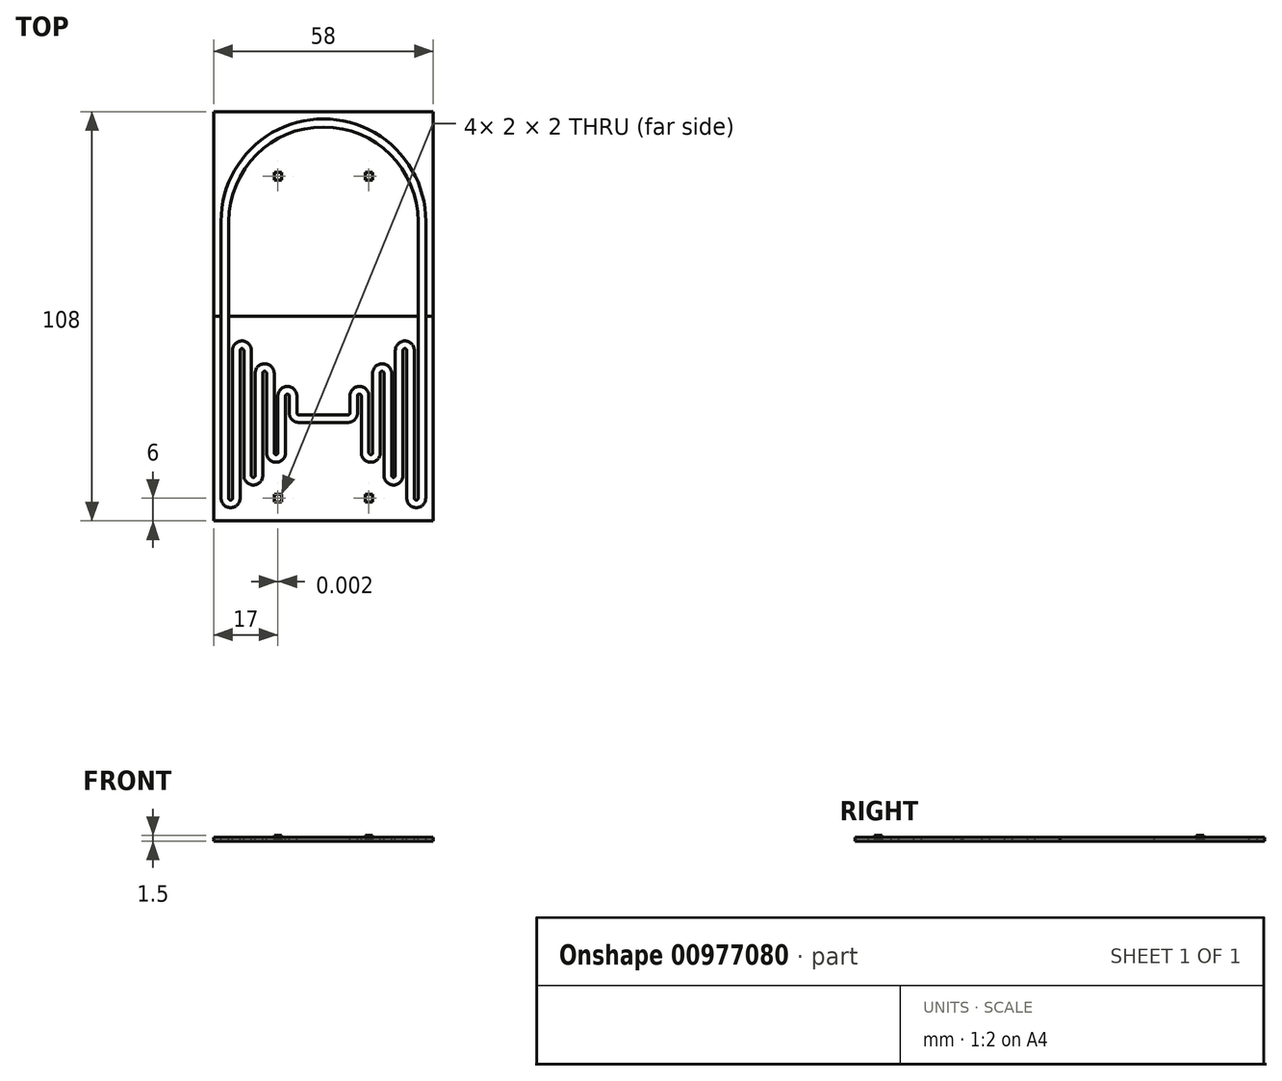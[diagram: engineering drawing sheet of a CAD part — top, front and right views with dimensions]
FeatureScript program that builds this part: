
annotation { "Feature Type Name" : "Feature", "Feature Type Description" : "" }
export const myFeature = defineFeature(function(context is Context, id is Id, definition is map)
    precondition{}
    {
        {
            var Q0;
            Q0=qCreatedBy(makeId("Top.planeOp"),FACE);
            var sketch = newSketch(context, id + "F0", { "sketchPlane" : qUnion([Q0])});
            skLineSegment(sketch, "E0.bottom", {"start": v(29, 27) * mm, "end": v(-29, 27) * mm});
            skLineSegment(sketch, "E0.top", {"start": v(29, -27) * mm, "end": v(-29, -27) * mm});
            skLineSegment(sketch, "E0.left", {"start": v(29, 27) * mm, "end": v(29, -27) * mm});
            skLineSegment(sketch, "E0.right", {"start": v(-29, 27) * mm, "end": v(-29, -27) * mm});
            skPoint(sketch, "E0.middle", {"position": v(0, 0) * mm});
            skSolve(sketch);
        }
        {
            var Q0;
            Q0=makeQuery(id+"F0.imprint","IMPRINT",FACE,{"disambiguationData":[TD([[makeQuery(id+"F0.imprint","IMPRINT",EDGE,{"derivedFrom":sQuery(id+"F0.wireOp",EDGE,"E0.bottom")}),1.0]])]});
            extrude(context, id + "F1", {"entities" : qUnion([Q0]), "depth" : 1 * mm, "offsetDistance" : 25 * mm});
        }
        {
            var Q0;
            Q0=makeQuery(id+"F1.opExtrude","CAP_FACE",FACE,{"disambiguationData":[OSD([sQuery(id+"F0.wireOp",EDGE,"E0.bottom"),sQuery(id+"F0.wireOp",EDGE,"E0.top"),sQuery(id+"F0.wireOp",EDGE,"E0.left"),sQuery(id+"F0.wireOp",EDGE,"E0.right")])],"isStart":false});
            var sketch = newSketch(context, id + "F2", { "sketchPlane" : qUnion([Q0])});
            skPoint(sketch, "E1.middle", {"position": v(-28, 0) * mm});
            skLineSegment(sketch, "E2.left", {"start": v(-27, 25) * mm, "end": v(-27, -21) * mm});
            skLineSegment(sketch, "E2.right", {"start": v(-25, 23.27) * mm, "end": v(-25, -21) * mm});
            skLineSegment(sketch, "E3.left", {"start": v(-25, 18) * mm, "end": v(-25, -21) * mm});
            skLineSegment(sketch, "E3.right", {"start": v(-24, 18) * mm, "end": v(-24, -21) * mm});
            skLineSegment(sketch, "E4.right", {"start": v(-22, 18) * mm, "end": v(-22, -21) * mm});
            skLineSegment(sketch, "E5.left", {"start": v(-21, 18) * mm, "end": v(-21, -15) * mm});
            skLineSegment(sketch, "E5.right", {"start": v(-19, 18) * mm, "end": v(-19, -15) * mm});
            skLineSegment(sketch, "E6.left", {"start": v(-18, 12) * mm, "end": v(-18, -15) * mm});
            skLineSegment(sketch, "E6.right", {"start": v(-16, 12) * mm, "end": v(-16, -15) * mm});
            skLineSegment(sketch, "E7.left", {"start": v(-15, 12) * mm, "end": v(-15, -9) * mm});
            skLineSegment(sketch, "E7.right", {"start": v(-13, 12) * mm, "end": v(-13, -9) * mm});
            skLineSegment(sketch, "E8.left", {"start": v(-12, 6) * mm, "end": v(-12, -9) * mm});
            skLineSegment(sketch, "E8.right", {"start": v(-10, 6) * mm, "end": v(-10, -9) * mm});
            skPoint(sketch, "E9.firstSnap0", {"position": v(-13, 1.5) * mm});
            skLineSegment(sketch, "E10.left", {"start": v(-9, 6) * mm, "end": v(-9, 1.5) * mm});
            skLineSegment(sketch, "E10.right", {"start": v(-7, 6) * mm, "end": v(-7, 1.5) * mm});
            skLineSegment(sketch, "E11.bottom", {"start": v(6.5, 1) * mm, "end": v(-6.5, 1) * mm});
            skLineSegment(sketch, "E11.top", {"start": v(6.5, -1) * mm, "end": v(-6.5, -1) * mm});
            skPoint(sketch, "E11.middle", {"position": v(0, 0) * mm});
            skArc(sketch, "E12", {"start": v(-9, 6) * mm, "mid": v(-9.5, 6.5) * mm, "end": v(-10, 6) * mm});
            skArc(sketch, "E13", {"start": v(-7, 6) * mm, "mid": v(-9.5, 8.5) * mm, "end": v(-12, 6) * mm});
            skArc(sketch, "E14", {"start": v(-13, -9) * mm, "mid": v(-12.5, -9.5) * mm, "end": v(-12, -9) * mm});
            skArc(sketch, "E15", {"start": v(-15, -9) * mm, "mid": v(-12.5, -11.5) * mm, "end": v(-10, -9) * mm});
            skArc(sketch, "E16", {"start": v(-15, 12) * mm, "mid": v(-15.5, 12.5) * mm, "end": v(-16, 12) * mm});
            skArc(sketch, "E17", {"start": v(-13, 12) * mm, "mid": v(-15.5, 14.5) * mm, "end": v(-18, 12) * mm});
            skArc(sketch, "E18", {"start": v(-19, -15) * mm, "mid": v(-18.5, -15.5) * mm, "end": v(-18, -15) * mm});
            skArc(sketch, "E19", {"start": v(-21, -15) * mm, "mid": v(-18.5, -17.5) * mm, "end": v(-16, -15) * mm});
            skArc(sketch, "E20", {"start": v(-21, 18) * mm, "mid": v(-21.5, 18.5) * mm, "end": v(-22, 18) * mm});
            skArc(sketch, "E21", {"start": v(-19, 18) * mm, "mid": v(-21.5, 20.5) * mm, "end": v(-24, 18) * mm});
            skArc(sketch, "E22", {"start": v(-25, -21) * mm, "mid": v(-24.5, -21.5) * mm, "end": v(-24, -21) * mm});
            skArc(sketch, "E23", {"start": v(-27, -21) * mm, "mid": v(-24.5, -23.5) * mm, "end": v(-22, -21) * mm});
            skArc(sketch, "E24", {"start": v(-7, 1.5) * mm, "mid": v(-6.86, 1.14) * mm, "end": v(-6.5, 1) * mm});
            skArc(sketch, "E25", {"start": v(-9, 1.5) * mm, "mid": v(-8.27, -0.27) * mm, "end": v(-6.5, -1) * mm});
            skLineSegment(sketch, "E26.left", {"start": v(25, 25) * mm, "end": v(25, -21) * mm});
            skLineSegment(sketch, "E26.right", {"start": v(27, 23.27) * mm, "end": v(27, -21) * mm});
            skLineSegment(sketch, "E27.right", {"start": v(25, 23.27) * mm, "end": v(25, -22.73) * mm});
            skLineSegment(sketch, "E28.left", {"start": v(22, 18) * mm, "end": v(22, -21) * mm});
            skLineSegment(sketch, "E28.right", {"start": v(24, 18) * mm, "end": v(24, -21) * mm});
            skLineSegment(sketch, "E29.left", {"start": v(19, 18) * mm, "end": v(19, -15) * mm});
            skLineSegment(sketch, "E29.right", {"start": v(21, 18) * mm, "end": v(21, -15) * mm});
            skLineSegment(sketch, "E30.left", {"start": v(16, 12) * mm, "end": v(16, -15) * mm});
            skLineSegment(sketch, "E30.right", {"start": v(18, 12) * mm, "end": v(18, -15) * mm});
            skLineSegment(sketch, "E31.right", {"start": v(16, 12) * mm, "end": v(16, -16.73) * mm});
            skLineSegment(sketch, "E32.left", {"start": v(13, 12) * mm, "end": v(13, -9) * mm});
            skLineSegment(sketch, "E32.right", {"start": v(15, 12) * mm, "end": v(15, -9) * mm});
            skLineSegment(sketch, "E33.left", {"start": v(10, 6) * mm, "end": v(10, -9) * mm});
            skLineSegment(sketch, "E33.right", {"start": v(12, 6) * mm, "end": v(12, -9) * mm});
            skLineSegment(sketch, "E34.left", {"start": v(7, 6) * mm, "end": v(7, 1.5) * mm});
            skLineSegment(sketch, "E34.right", {"start": v(9, 6) * mm, "end": v(9, 1.5) * mm});
            skArc(sketch, "E35", {"start": v(6.5, 1) * mm, "mid": v(6.85, 1.14) * mm, "end": v(7, 1.5) * mm});
            skArc(sketch, "E36", {"start": v(6.5, -1) * mm, "mid": v(8.26, -0.27) * mm, "end": v(9, 1.5) * mm});
            skArc(sketch, "E37", {"start": v(22, -21) * mm, "mid": v(24.5, -23.5) * mm, "end": v(27, -21) * mm});
            skArc(sketch, "E38", {"start": v(24, -21) * mm, "mid": v(24.5, -21.5) * mm, "end": v(25, -21) * mm});
            skArc(sketch, "E39", {"start": v(18, -15) * mm, "mid": v(18.5, -15.5) * mm, "end": v(19, -15) * mm});
            skArc(sketch, "E40", {"start": v(16, -15) * mm, "mid": v(18.5, -17.5) * mm, "end": v(21, -15) * mm});
            skArc(sketch, "E41", {"start": v(12, -9) * mm, "mid": v(12.5, -9.5) * mm, "end": v(13, -9) * mm});
            skArc(sketch, "E42", {"start": v(10, -9) * mm, "mid": v(12.5, -11.5) * mm, "end": v(15, -9) * mm});
            skArc(sketch, "E43", {"start": v(22, 18) * mm, "mid": v(21.5, 18.5) * mm, "end": v(21, 18) * mm});
            skArc(sketch, "E44", {"start": v(24, 18) * mm, "mid": v(21.5, 20.5) * mm, "end": v(19, 18) * mm});
            skArc(sketch, "E45", {"start": v(16, 12) * mm, "mid": v(15.5, 12.5) * mm, "end": v(15, 12) * mm});
            skArc(sketch, "E46", {"start": v(18, 12) * mm, "mid": v(15.5, 14.5) * mm, "end": v(13, 12) * mm});
            skArc(sketch, "E47", {"start": v(10, 6) * mm, "mid": v(9.5, 6.5) * mm, "end": v(9, 6) * mm});
            skArc(sketch, "E48", {"start": v(12, 6) * mm, "mid": v(9.5, 8.5) * mm, "end": v(7, 6) * mm});
            skLineSegment(sketch, "E49.top", {"start": v(-27, 27) * mm, "end": v(-25, 27) * mm});
            skLineSegment(sketch, "E49.left", {"start": v(-27, 25) * mm, "end": v(-27, 27) * mm});
            skLineSegment(sketch, "E49.right", {"start": v(-25, 25) * mm, "end": v(-25, 27) * mm});
            skLineSegment(sketch, "E50.top", {"start": v(25, 27) * mm, "end": v(27, 27) * mm});
            skLineSegment(sketch, "E50.left", {"start": v(25, 23.27) * mm, "end": v(25, 27) * mm});
            skLineSegment(sketch, "E50.right", {"start": v(27, 25) * mm, "end": v(27, 27) * mm});
            skLineSegment(sketch, "E51", {"start": v(27, 25) * mm, "end": v(27, 23.27) * mm});
            skLineSegment(sketch, "E52", {"start": v(-25, 25) * mm, "end": v(-25, 23.27) * mm});
            skSolve(sketch);
        }
        {
            var Q0;
            Q0=makeQuery(id+"F2.imprint","IMPRINT",FACE,{"disambiguationData":[TD([[makeQuery(id+"F2.imprint","IMPRINT",EDGE,{"derivedFrom":sQuery(id+"F2.wireOp",EDGE,"E2.left")}),1.0]])]});
            extrude(context, id + "F3", {"entities" : qUnion([Q0]), "operationType" : NewBodyOperationType.REMOVE, "oppositeDirection" : true, "depth" : 1 * mm, "offsetDistance" : 25 * mm});
        }
        {
            var Q0;
            Q0=qCreatedBy(makeId("Top.planeOp"),FACE);
            var sketch = newSketch(context, id + "F4", { "sketchPlane" : qUnion([Q0])});
            skLineSegment(sketch, "E53.bottom", {"start": v(-29, 27) * mm, "end": v(29, 27) * mm});
            skLineSegment(sketch, "E53.top", {"start": v(-29, 81) * mm, "end": v(29, 81) * mm});
            skLineSegment(sketch, "E53.left", {"start": v(-29, 27) * mm, "end": v(-29, 81) * mm});
            skLineSegment(sketch, "E53.right", {"start": v(29, 27) * mm, "end": v(29, 81) * mm});
            skSolve(sketch);
        }
        {
            var Q0;
            Q0=makeQuery(id+"F4.imprint","IMPRINT",FACE,{"disambiguationData":[TD([[makeQuery(id+"F4.imprint","IMPRINT",EDGE,{"derivedFrom":sQuery(id+"F4.wireOp",EDGE,"E53.bottom")}),1.0]])]});
            extrude(context, id + "F5", {"entities" : qUnion([Q0]), "depth" : 1 * mm, "offsetDistance" : 25 * mm});
        }
        {
            var Q0;
            Q0=makeQuery(id+"F5.opExtrude","CAP_FACE",FACE,{"disambiguationData":[OSD([sQuery(id+"F4.wireOp",EDGE,"E53.bottom"),sQuery(id+"F4.wireOp",EDGE,"E53.top"),sQuery(id+"F4.wireOp",EDGE,"E53.left"),sQuery(id+"F4.wireOp",EDGE,"E53.right")])],"isStart":false});
            var sketch = newSketch(context, id + "F6", { "sketchPlane" : qUnion([Q0])});
            skLineSegment(sketch, "E54.bottom", {"start": v(-27, 27) * mm, "end": v(-25, 27) * mm});
            skLineSegment(sketch, "E54.top", {"start": v(-27, 52) * mm, "end": v(-25, 52) * mm});
            skLineSegment(sketch, "E54.left", {"start": v(-27, 27) * mm, "end": v(-27, 52) * mm});
            skLineSegment(sketch, "E54.right", {"start": v(-25, 27) * mm, "end": v(-25, 52) * mm});
            skLineSegment(sketch, "E55.bottom", {"start": v(27, 27) * mm, "end": v(25, 27) * mm});
            skLineSegment(sketch, "E55.top", {"start": v(27, 52) * mm, "end": v(25, 52) * mm});
            skLineSegment(sketch, "E55.left", {"start": v(27, 27) * mm, "end": v(27, 52) * mm});
            skLineSegment(sketch, "E55.right", {"start": v(25, 27) * mm, "end": v(25, 52) * mm});
            skArc(sketch, "E56", {"start": v(25, 52) * mm, "mid": v(0, 77) * mm, "end": v(-25, 52) * mm});
            skArc(sketch, "E57", {"start": v(27, 52) * mm, "mid": v(0, 79.13) * mm, "end": v(-27, 52) * mm});
            skPoint(sketch, "E57.startSnap0", {"position": v(27, 39.5) * mm});
            skSolve(sketch);
        }
        {
            var Q0;
            Q0=qSketchRegion(id+"F6",true);
            extrude(context, id + "F7", {"entities" : qUnion([Q0]), "operationType" : NewBodyOperationType.REMOVE, "oppositeDirection" : true, "depth" : 1 * mm, "offsetDistance" : 25 * mm});
        }
        {
            var Q0;
            Q0=makeQuery(id+"F2.imprint","IMPRINT",FACE,{"disambiguationData":[TD([[makeQuery(id+"F2.imprint","IMPRINT",EDGE,{"derivedFrom":sQuery(id+"F2.wireOp",EDGE,"E2.left")}),-1.0]])]});
            var sketch = newSketch(context, id + "F8", { "sketchPlane" : qUnion([Q0])});
            skLineSegment(sketch, "E58.bottom", {"start": v(-13, -20) * mm, "end": v(-11, -20) * mm});
            skLineSegment(sketch, "E58.top", {"start": v(-13, -22) * mm, "end": v(-11, -22) * mm});
            skLineSegment(sketch, "E58.left", {"start": v(-13, -20) * mm, "end": v(-13, -22) * mm});
            skLineSegment(sketch, "E58.right", {"start": v(-11, -20) * mm, "end": v(-11, -22) * mm});
            skLineSegment(sketch, "E59.bottom", {"start": v(11, -20) * mm, "end": v(13, -20) * mm});
            skLineSegment(sketch, "E59.top", {"start": v(11, -22) * mm, "end": v(13, -22) * mm});
            skLineSegment(sketch, "E59.left", {"start": v(11, -20) * mm, "end": v(11, -22) * mm});
            skLineSegment(sketch, "E59.right", {"start": v(13, -20) * mm, "end": v(13, -22) * mm});
            skSolve(sketch);
        }
        {
            var Q0;
            Q0 = qSketchRegion(id + "F8", true);
            extrude(context, id + "F9", {"entities" : qUnion([Q0]), "operationType" : NewBodyOperationType.ADD, "depth" : 0.5 * mm, "offsetDistance" : 25 * mm});
        }
        {
            var Q0;
            {var subQ0=sQuery(id+"F4.wireOp",EDGE,"E53.bottom");Q0=makeQuery(id+"F7.boolean.opBoolean","SPLIT",FACE,{"disambiguationData":[TD([makeQuery(id+"F7.opExtrude","SWEPT_FACE",FACE,{"disambiguationData":[OSD([sQuery(id+"F6.wireOp",EDGE,"E55.top")])]})])],"derivedFrom":makeQuery(id+"F5.opExtrude","CAP_FACE",FACE,{"disambiguationData":[OSD([subQ0,sQuery(id+"F4.wireOp",EDGE,"E53.top"),sQuery(id+"F4.wireOp",EDGE,"E53.left"),sQuery(id+"F4.wireOp",EDGE,"E53.right")])],"isStart":false})});}
            var sketch = newSketch(context, id + "F10", { "sketchPlane" : qUnion([Q0])});
            skLineSegment(sketch, "E60.bottom", {"start": v(-13, 65) * mm, "end": v(-11, 65) * mm});
            skLineSegment(sketch, "E60.top", {"start": v(-13, 63) * mm, "end": v(-11, 63) * mm});
            skLineSegment(sketch, "E60.left", {"start": v(-13, 65) * mm, "end": v(-13, 63) * mm});
            skLineSegment(sketch, "E60.right", {"start": v(-11, 65) * mm, "end": v(-11, 63) * mm});
            skLineSegment(sketch, "E61.bottom", {"start": v(11, 65) * mm, "end": v(13, 65) * mm});
            skLineSegment(sketch, "E61.top", {"start": v(11, 63) * mm, "end": v(13, 63) * mm});
            skLineSegment(sketch, "E61.left", {"start": v(11, 65) * mm, "end": v(11, 63) * mm});
            skLineSegment(sketch, "E61.right", {"start": v(13, 65) * mm, "end": v(13, 63) * mm});
            skSolve(sketch);
        }
        {
            var Q0;
            Q0 = qSketchRegion(id + "F10", true);
            extrude(context, id + "F11", {"entities" : qUnion([Q0]), "operationType" : NewBodyOperationType.ADD, "depth" : 0.5 * mm, "offsetDistance" : 25 * mm});
        }
        {
            var Q0;
            {var subQ0=sQuery(id+"F4.wireOp",EDGE,"E53.bottom");Q0=makeQuery(id+"F7.boolean.opBoolean","SPLIT",FACE,{"disambiguationData":[TD([makeQuery(id+"F7.opExtrude","SWEPT_FACE",FACE,{"disambiguationData":[OSD([sQuery(id+"F6.wireOp",EDGE,"E55.top")])]})])],"derivedFrom":makeQuery(id+"F5.opExtrude","CAP_FACE",FACE,{"disambiguationData":[OSD([subQ0,sQuery(id+"F4.wireOp",EDGE,"E53.top"),sQuery(id+"F4.wireOp",EDGE,"E53.left"),sQuery(id+"F4.wireOp",EDGE,"E53.right")])],"isStart":true})});}
            var sketch = newSketch(context, id + "F12", { "sketchPlane" : qUnion([Q0])});
            skLineSegment(sketch, "E62.bottom", {"start": v(-13, -63) * mm, "end": v(-11, -63) * mm});
            skLineSegment(sketch, "E62.top", {"start": v(-13, -65) * mm, "end": v(-11, -65) * mm});
            skLineSegment(sketch, "E62.left", {"start": v(-13, -63) * mm, "end": v(-13, -65) * mm});
            skLineSegment(sketch, "E62.right", {"start": v(-11, -63) * mm, "end": v(-11, -65) * mm});
            skLineSegment(sketch, "E63.bottom", {"start": v(11, -63) * mm, "end": v(13, -63) * mm});
            skLineSegment(sketch, "E63.top", {"start": v(11, -65) * mm, "end": v(13, -65) * mm});
            skLineSegment(sketch, "E63.left", {"start": v(11, -63) * mm, "end": v(11, -65) * mm});
            skLineSegment(sketch, "E63.right", {"start": v(13, -63) * mm, "end": v(13, -65) * mm});
            skSolve(sketch);
        }
        {
            var Q0;
            Q0=makeQuery(id+"F12.imprint","IMPRINT",FACE,{"disambiguationData":[TD([[makeQuery(id+"F12.imprint","IMPRINT",EDGE,{"derivedFrom":sQuery(id+"F12.wireOp",EDGE,"E62.bottom")}),-1.0]])]});
            var Q1;
            Q1=makeQuery(id+"F12.imprint","IMPRINT",FACE,{"disambiguationData":[TD([[makeQuery(id+"F12.imprint","IMPRINT",EDGE,{"derivedFrom":sQuery(id+"F12.wireOp",EDGE,"E63.bottom")}),-1.0]])]});
            extrude(context, id + "F13", {"entities" : qUnion([Q0, Q1]), "operationType" : NewBodyOperationType.REMOVE, "oppositeDirection" : true, "depth" : 0.5 * mm, "offsetDistance" : 25 * mm});
        }
        {
            var Q0;
            {var subQ0=sQuery(id+"F0.wireOp",EDGE,"E0.left");var subQ1=sQuery(id+"F0.wireOp",EDGE,"E0.top");var subQ2=sQuery(id+"F0.wireOp",EDGE,"E0.right");var subQ3=sQuery(id+"F0.wireOp",EDGE,"E0.bottom");Q0=makeQuery(id+"F3.boolean.opBoolean","SPLIT",FACE,{"disambiguationData":[TD([makeQuery(id+"F1.opExtrude","SWEPT_FACE",FACE,{"disambiguationData":[OSD([subQ1])]})])],"derivedFrom":makeQuery(id+"F1.opExtrude","CAP_FACE",FACE,{"disambiguationData":[OSD([subQ3,subQ1,subQ0,subQ2])],"isStart":true})});}
            var sketch = newSketch(context, id + "F14", { "sketchPlane" : qUnion([Q0])});
            skLineSegment(sketch, "E64.bottom", {"start": v(-13, 22) * mm, "end": v(-11, 22) * mm});
            skLineSegment(sketch, "E64.top", {"start": v(-13, 20) * mm, "end": v(-11, 20) * mm});
            skLineSegment(sketch, "E64.left", {"start": v(-13, 22) * mm, "end": v(-13, 20) * mm});
            skLineSegment(sketch, "E64.right", {"start": v(-11, 22) * mm, "end": v(-11, 20) * mm});
            skLineSegment(sketch, "E65.bottom", {"start": v(11, 22) * mm, "end": v(13, 22) * mm});
            skLineSegment(sketch, "E65.top", {"start": v(11, 20) * mm, "end": v(13, 20) * mm});
            skLineSegment(sketch, "E65.left", {"start": v(11, 22) * mm, "end": v(11, 20) * mm});
            skLineSegment(sketch, "E65.right", {"start": v(13, 22) * mm, "end": v(13, 20) * mm});
            skSolve(sketch);
        }
        {
            var Q0;
            Q0=makeQuery(id+"F14.imprint","IMPRINT",FACE,{"disambiguationData":[TD([[makeQuery(id+"F14.imprint","IMPRINT",EDGE,{"derivedFrom":sQuery(id+"F14.wireOp",EDGE,"E64.bottom")}),-1.0]])]});
            var Q1;
            Q1=makeQuery(id+"F14.imprint","IMPRINT",FACE,{"disambiguationData":[TD([[makeQuery(id+"F14.imprint","IMPRINT",EDGE,{"derivedFrom":sQuery(id+"F14.wireOp",EDGE,"E65.bottom")}),-1.0]])]});
            extrude(context, id + "F15", {"entities" : qUnion([Q0, Q1]), "operationType" : NewBodyOperationType.REMOVE, "oppositeDirection" : true, "depth" : 0.5 * mm, "offsetDistance" : 25 * mm});
        }
    });
